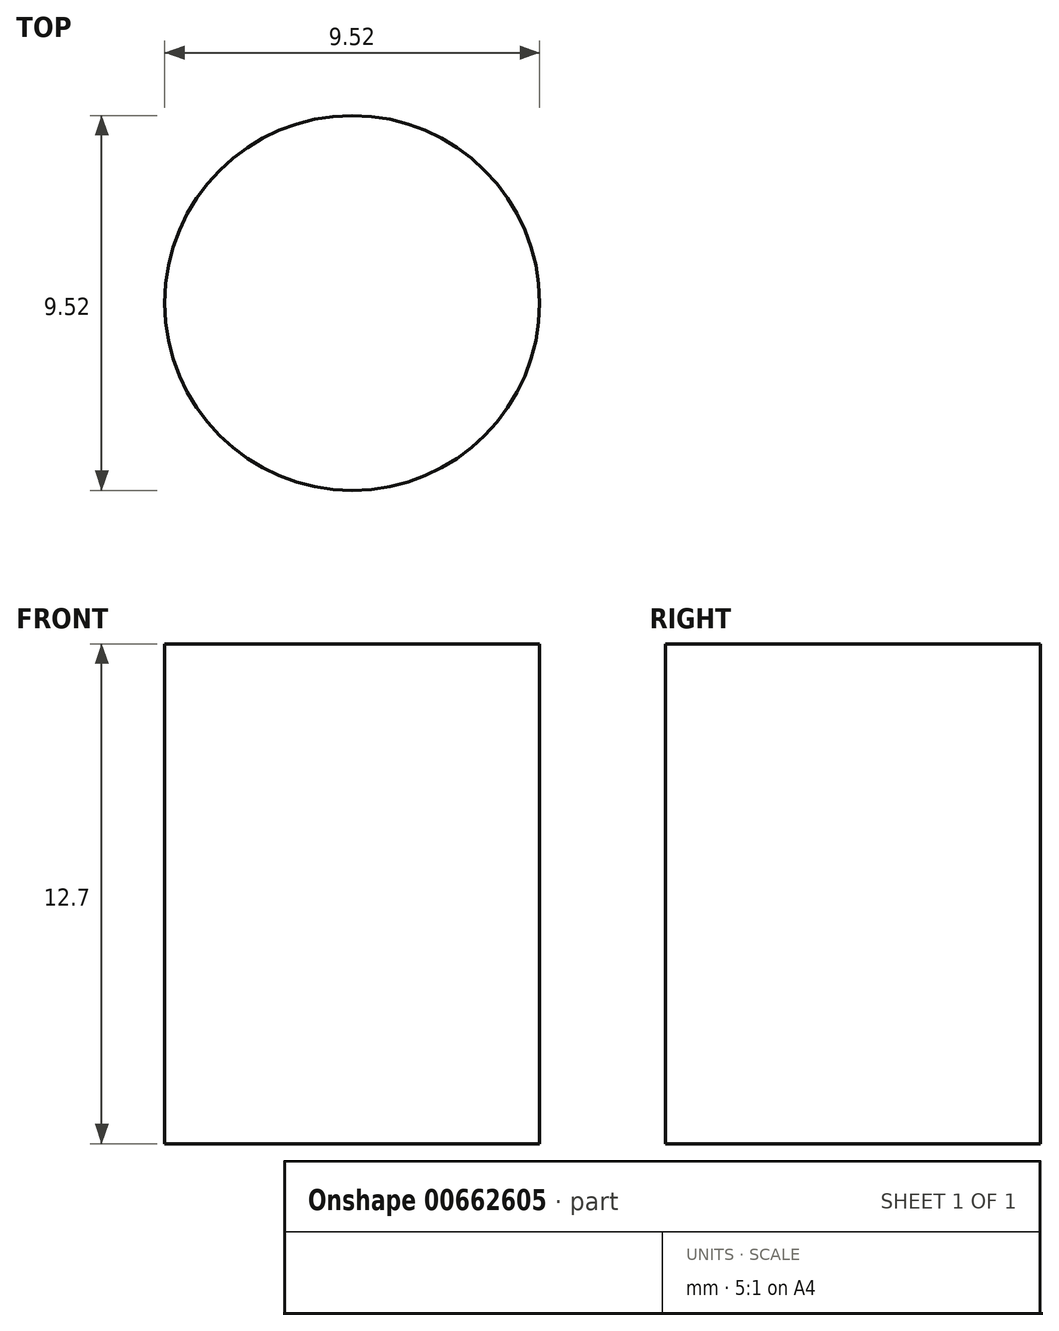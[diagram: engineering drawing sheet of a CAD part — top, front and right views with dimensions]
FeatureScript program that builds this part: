
annotation { "Feature Type Name" : "Feature", "Feature Type Description" : "" }
export const myFeature = defineFeature(function(context is Context, id is Id, definition is map)
    precondition{}
    {
        {
            var Q0;
            Q0=qCreatedBy(makeId("Top.planeOp"),FACE);
            var sketch = newSketch(context, id + "F0", { "sketchPlane" : qUnion([Q0])});
            skCircle(sketch, "E0", {"center": v(0, 0) * mm, "radius": 4.76 * mm});
            skSolve(sketch);
        }
        {
            var Q0;
            Q0=makeQuery(id+"F0.imprint","IMPRINT",FACE,{"disambiguationData":[TD([[makeQuery(id+"F0.imprint","IMPRINT",EDGE,{"derivedFrom":sQuery(id+"F0.wireOp",EDGE,"E0")}),1.0]])]});
            extrude(context, id + "F1", {"entities" : qUnion([Q0]), "depth" : 12.7 * mm, "offsetDistance" : 25.4 * mm});
        }
    });
